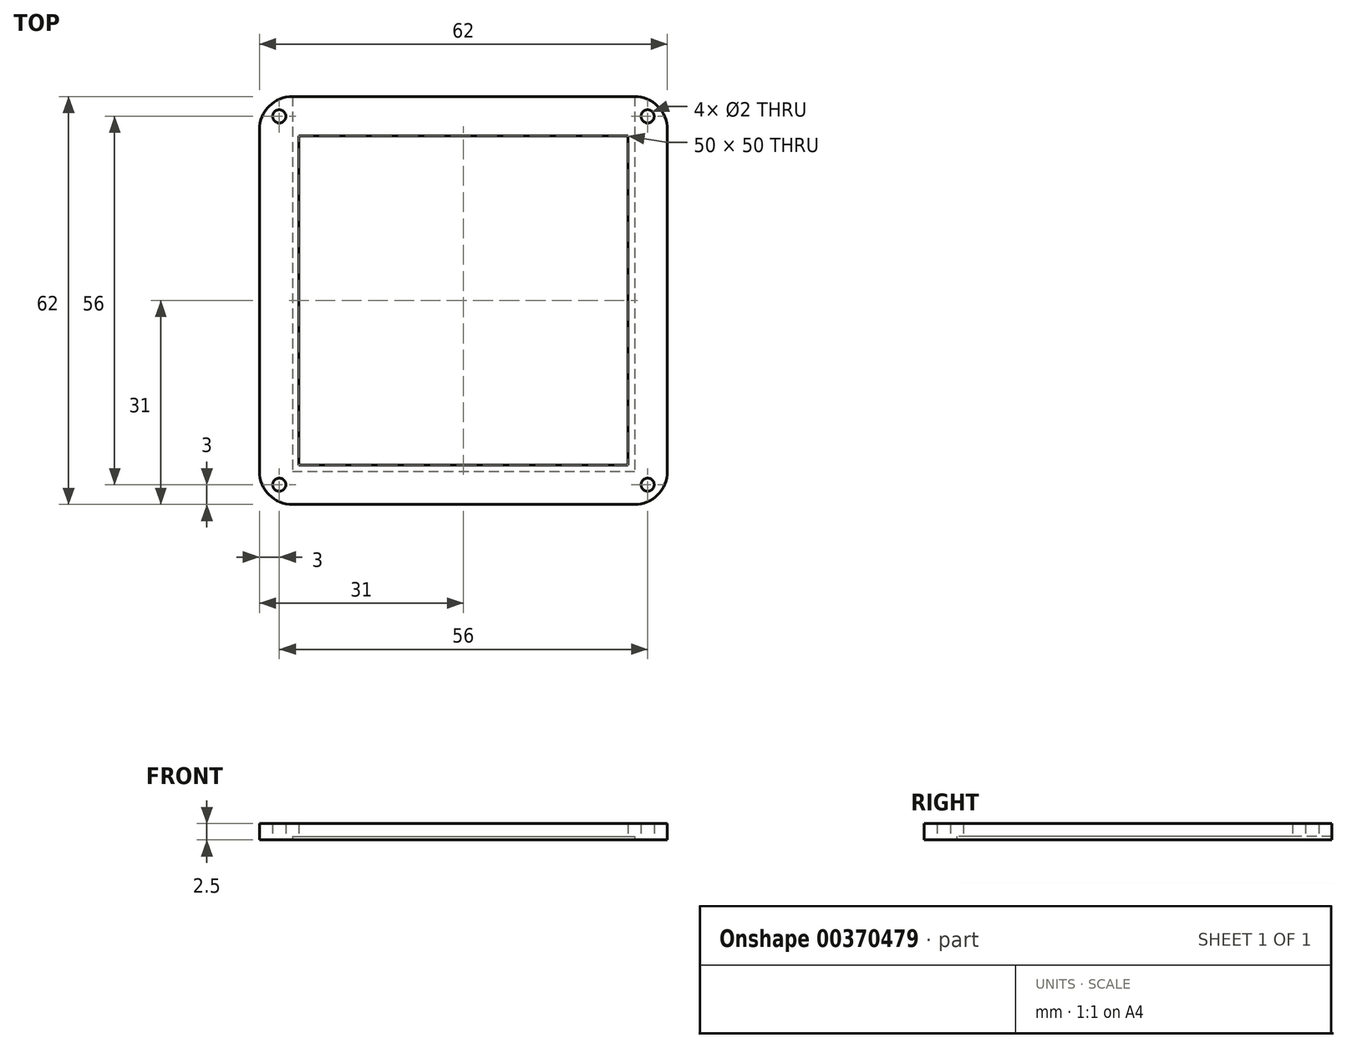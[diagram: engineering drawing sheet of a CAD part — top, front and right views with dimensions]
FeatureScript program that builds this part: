
annotation { "Feature Type Name" : "Feature", "Feature Type Description" : "" }
export const myFeature = defineFeature(function(context is Context, id is Id, definition is map)
    precondition{}
    {
        {
            var Q0;
            Q0=qCreatedBy(makeId("Top.planeOp"),FACE);
            var sketch = newSketch(context, id + "F0", { "sketchPlane" : qUnion([Q0])});
            skLineSegment(sketch, "E0.bottom", {"start": v(5, 0) * mm, "end": v(57, 0) * mm});
            skLineSegment(sketch, "E0.top", {"start": v(5, -62) * mm, "end": v(57, -62) * mm});
            skLineSegment(sketch, "E0.left", {"start": v(0, -5) * mm, "end": v(0, -57) * mm});
            skLineSegment(sketch, "E0.right", {"start": v(62, -5) * mm, "end": v(62, -57) * mm});
            skPoint(sketch, "E1.visualSharp", {"position": v(0, 0) * mm});
            skArc(sketch, "E1.filletArc", {"start": v(5, 0) * mm, "mid": v(1.46, -1.46) * mm, "end": v(0, -5) * mm});
            skPoint(sketch, "E2.visualSharp", {"position": v(62, 0) * mm});
            skArc(sketch, "E2.filletArc", {"start": v(62, -5) * mm, "mid": v(60.54, -1.46) * mm, "end": v(57, 0) * mm});
            skPoint(sketch, "E3.visualSharp", {"position": v(62, -62) * mm});
            skArc(sketch, "E3.filletArc", {"start": v(57, -62) * mm, "mid": v(60.54, -60.54) * mm, "end": v(62, -57) * mm});
            skPoint(sketch, "E4.visualSharp", {"position": v(0, -62) * mm});
            skArc(sketch, "E4.filletArc", {"start": v(0, -57) * mm, "mid": v(1.46, -60.54) * mm, "end": v(5, -62) * mm});
            skLineSegment(sketch, "E5.bottom", {"start": v(5, -5) * mm, "end": v(57, -5) * mm});
            skLineSegment(sketch, "E5.top", {"start": v(5, -57) * mm, "end": v(57, -57) * mm});
            skLineSegment(sketch, "E5.left", {"start": v(5, -5) * mm, "end": v(5, -57) * mm});
            skLineSegment(sketch, "E5.right", {"start": v(57, -5) * mm, "end": v(57, -57) * mm});
            skLineSegment(sketch, "E6.0", {"start": v(6, -6) * mm, "end": v(56, -6) * mm});
            skLineSegment(sketch, "E6.1", {"start": v(6, -6) * mm, "end": v(6, -56) * mm});
            skLineSegment(sketch, "E6.2", {"start": v(6, -56) * mm, "end": v(56, -56) * mm});
            skLineSegment(sketch, "E6.3", {"start": v(56, -6) * mm, "end": v(56, -56) * mm});
            skLineSegment(sketch, "E7", {"start": v(0, 0) * mm, "end": v(6, -6) * mm, "construction": true});
            skPoint(sketch, "E8", {"position": v(3, -3) * mm});
            skLineSegment(sketch, "E9", {"start": v(62, 0) * mm, "end": v(56, -6) * mm, "construction": true});
            skLineSegment(sketch, "E10", {"start": v(62, -62) * mm, "end": v(56, -56) * mm, "construction": true});
            skLineSegment(sketch, "E11", {"start": v(6, -56) * mm, "end": v(0, -62) * mm, "construction": true});
            skCircle(sketch, "E12", {"center": v(3, -3) * mm, "radius": 1 * mm});
            skCircle(sketch, "E13", {"center": v(59, -3) * mm, "radius": 1 * mm});
            skCircle(sketch, "E14", {"center": v(59, -59) * mm, "radius": 1 * mm});
            skCircle(sketch, "E15", {"center": v(3, -59) * mm, "radius": 1 * mm});
            skSolve(sketch);
        }
        {
            var Q0;
            Q0=makeQuery(id+"F0.imprint","IMPRINT",FACE,{"disambiguationData":[TD([[makeQuery(id+"F0.imprint","IMPRINT",EDGE,{"derivedFrom":sQuery(id+"F0.wireOp",EDGE,"E0.bottom")}),-1.0]])]});
            var Q1;
            Q1=makeQuery(id+"F0.imprint","IMPRINT",FACE,{"disambiguationData":[TD([[makeQuery(id+"F0.imprint","IMPRINT",EDGE,{"derivedFrom":sQuery(id+"F0.wireOp",EDGE,"E5.bottom")}),-1.0]])]});
            extrude(context, id + "F1", {"entities" : qUnion([Q0, Q1]), "depth" : 2.5 * mm});
        }
        {
            var Q0;
            Q0=makeQuery(id+"F0.imprint","IMPRINT",FACE,{"disambiguationData":[TD([[makeQuery(id+"F0.imprint","IMPRINT",EDGE,{"derivedFrom":sQuery(id+"F0.wireOp",EDGE,"E5.bottom")}),-1.0]])]});
            extrude(context, id + "F2", {"entities" : qUnion([Q0]), "operationType" : NewBodyOperationType.REMOVE, "depth" : 0.5 * mm});
        }
        {
            var Q0;
            Q0=makeQuery(id+"F0.imprint","IMPRINT",FACE,{"disambiguationData":[TD([[makeQuery(id+"F0.imprint","IMPRINT",EDGE,{"derivedFrom":sQuery(id+"F0.wireOp",EDGE,"E0.bottom")}),-1.0]])]});
            var sketch = newSketch(context, id + "F3", { "sketchPlane" : qUnion([Q0])});
            skLineSegment(sketch, "E16.bottom", {"start": v(5, -5) * mm, "end": v(57, -5) * mm});
            skLineSegment(sketch, "E16.top", {"start": v(5, 0) * mm, "end": v(57, 0) * mm});
            skLineSegment(sketch, "E16.left", {"start": v(5, -5) * mm, "end": v(5, 0) * mm});
            skLineSegment(sketch, "E16.right", {"start": v(57, -5) * mm, "end": v(57, 0) * mm});
            skSolve(sketch);
        }
        {
            var Q0;
            Q0=makeQuery(id+"F3.imprint","IMPRINT",FACE,{"disambiguationData":[TD([[makeQuery(id+"F3.imprint","IMPRINT",EDGE,{"derivedFrom":sQuery(id+"F3.wireOp",EDGE,"E16.bottom")}),1.0]])]});
            extrude(context, id + "F4", {"entities" : qUnion([Q0]), "operationType" : NewBodyOperationType.REMOVE, "depth" : 0.5 * mm});
        }
    });
